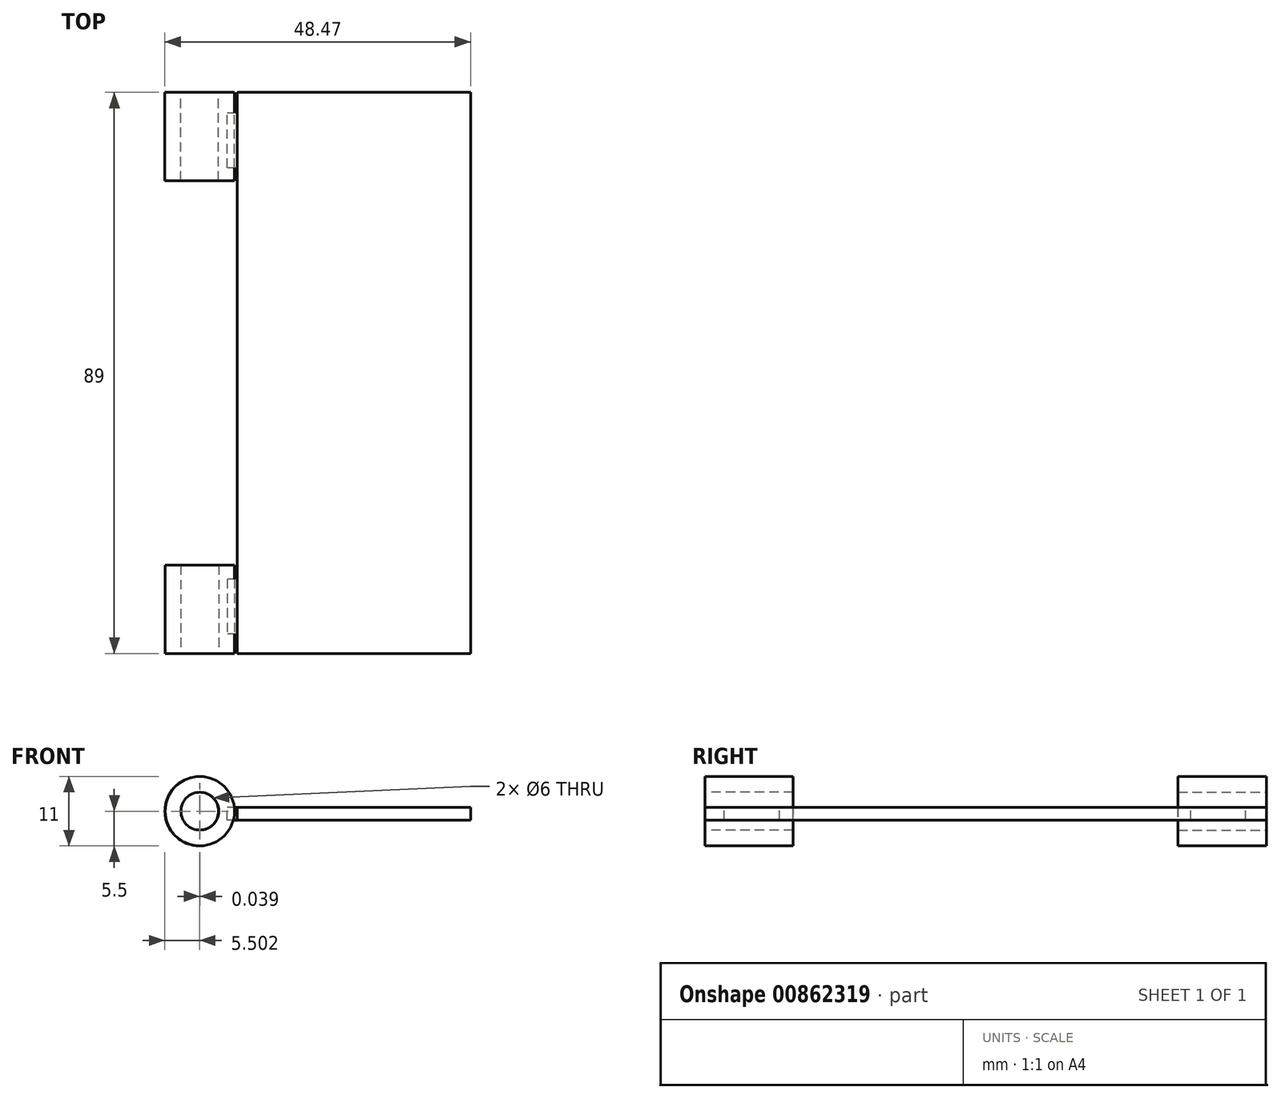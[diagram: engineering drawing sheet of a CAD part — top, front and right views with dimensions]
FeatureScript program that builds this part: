
annotation { "Feature Type Name" : "Feature", "Feature Type Description" : "" }
export const myFeature = defineFeature(function(context is Context, id is Id, definition is map)
    precondition{}
    {
        {
            var Q0;
            Q0=qCreatedBy(makeId("Top.planeOp"),FACE);
            var sketch = newSketch(context, id + "F0", { "sketchPlane" : qUnion([Q0])});
            skLineSegment(sketch, "E0.bottom", {"start": v(0, 0) * mm, "end": v(37, 0) * mm});
            skLineSegment(sketch, "E0.top", {"start": v(0, -89) * mm, "end": v(37, -89) * mm});
            skLineSegment(sketch, "E0.left", {"start": v(0, 0) * mm, "end": v(0, -89) * mm});
            skLineSegment(sketch, "E0.right", {"start": v(37, 0) * mm, "end": v(37, -89) * mm});
            skSolve(sketch);
        }
        {
            var Q0;
            Q0 = qSketchRegion(id + "F0", true);
            extrude(context, id + "F1", {"entities" : qUnion([Q0]), "depth" : 2 * mm, "offsetDistance" : 25 * mm});
        }
        {
            var Q0;
            Q0=makeQuery(id+"F1.opExtrude","SWEPT_FACE",FACE,{"disambiguationData":[OSD([sQuery(id+"F0.wireOp",EDGE,"E0.top")])]});
            var sketch = newSketch(context, id + "F2", { "sketchPlane" : qUnion([Q0])});
            skCircle(sketch, "E1", {"center": v(-5.93, 1.42) * mm, "radius": 5.5 * mm});
            skCircle(sketch, "E2", {"center": v(-5.93, 1.42) * mm, "radius": 3 * mm});
            skLineSegment(sketch, "E3", {"start": v(0, 1.42) * mm, "end": v(0, 2) * mm, "construction": true});
            skSolve(sketch);
        }
        {
            var Q0;
            Q0 = qSketchRegion(id + "F2", true);
            extrude(context, id + "F3", {"entities" : qUnion([Q0]), "oppositeDirection" : true, "depth" : 14 * mm, "offsetDistance" : 25 * mm});
        }
        {
            var Q0;
            Q0=makeQuery(id+"F1.opExtrude","CAP_FACE",FACE,{"disambiguationData":[OSD([sQuery(id+"F0.wireOp",EDGE,"E0.bottom"),sQuery(id+"F0.wireOp",EDGE,"E0.top"),sQuery(id+"F0.wireOp",EDGE,"E0.left"),sQuery(id+"F0.wireOp",EDGE,"E0.right")])],"isStart":false});
            var sketch = newSketch(context, id + "F4", { "sketchPlane" : qUnion([Q0])});
            skLineSegment(sketch, "E4", {"start": v(0, -85.93) * mm, "end": v(-1.59, -85.93) * mm});
            skLineSegment(sketch, "E5", {"start": v(0, -77.2) * mm, "end": v(-1.59, -77.2) * mm});
            skLineSegment(sketch, "E6", {"start": v(-1.59, -77.2) * mm, "end": v(-1.59, -85.93) * mm});
            skLineSegment(sketch, "E7", {"start": v(0, -44.5) * mm, "end": v(37, -44.5) * mm, "construction": true});
            skLineSegment(sketch, "E8.MirrorCS", {"start": v(-1.59, -11.8) * mm, "end": v(-1.59, -3.07) * mm});
            skLineSegment(sketch, "E9.MirrorCS", {"start": v(0, -11.8) * mm, "end": v(-1.59, -11.8) * mm});
            skLineSegment(sketch, "E10.MirrorCS", {"start": v(0, -3.07) * mm, "end": v(-1.59, -3.07) * mm});
            skSolve(sketch);
        }
        {
            var Q0;
            Q0 = qSketchRegion(id + "F4", true);
            var Q1;
            {var subQ0=sQuery(id+"F4.wireOp",EDGE,"E4");Q1=makeQuery(id+"F4.imprint","IMPRINT",FACE,{"disambiguationData":[TD([[makeQuery(id+"F4.imprint","IMPRINT",EDGE,{"derivedFrom":subQ0}),-1.0]])]});}
            extrude(context, id + "F5", {"entities" : qUnion([Q0, Q1]), "oppositeDirection" : true, "depth" : 2 * mm, "offsetDistance" : 25 * mm});
        }
        {
            var Q0;
            Q0=makeQuery(id+"F1.opExtrude","SWEPT_FACE",FACE,{"disambiguationData":[OSD([sQuery(id+"F0.wireOp",EDGE,"E0.bottom")])]});
            var sketch = newSketch(context, id + "F6", { "sketchPlane" : qUnion([Q0])});
            skLineSegment(sketch, "E11", {"start": v(0, 2) * mm, "end": v(0, 1.42) * mm, "construction": true});
            skPoint(sketch, "E11.endSnap0", {"position": v(0, 1) * mm});
            skCircle(sketch, "E12", {"center": v(5.97, 1.42) * mm, "radius": 5.5 * mm});
            skCircle(sketch, "E13", {"center": v(5.97, 1.42) * mm, "radius": 3 * mm});
            skSolve(sketch);
        }
        {
            var Q0;
            Q0 = qSketchRegion(id + "F6", true);
            var Q1;
            Q1 = qSketchRegion(id + "F4", true);
            extrude(context, id + "F7", {"entities" : qUnion([Q0, Q1]), "oppositeDirection" : true, "depth" : 14 * mm, "offsetDistance" : 25 * mm});
        }
        {
            var Q0;
            Q0=makeQuery(id+"F1.opExtrude","CAP_FACE",FACE,{"disambiguationData":[OSD([sQuery(id+"F0.wireOp",EDGE,"E0.bottom"),sQuery(id+"F0.wireOp",EDGE,"E0.top"),sQuery(id+"F0.wireOp",EDGE,"E0.left"),sQuery(id+"F0.wireOp",EDGE,"E0.right")])],"isStart":false});
            var sketch = newSketch(context, id + "F8", { "sketchPlane" : qUnion([Q0])});
            skLineSegment(sketch, "E14", {"start": v(0, -11.98) * mm, "end": v(-1.6, -11.98) * mm});
            skLineSegment(sketch, "E15", {"start": v(-1.6, -11.98) * mm, "end": v(-1.6, -3.24) * mm});
            skLineSegment(sketch, "E16", {"start": v(-1.6, -3.24) * mm, "end": v(0, -3.24) * mm});
            skSolve(sketch);
        }
        {
            var Q0;
            Q0 = qSketchRegion(id + "F8", true);
            var Q1;
            {var subQ0=sQuery(id+"F8.wireOp",EDGE,"E14");Q1=makeQuery(id+"F8.imprint","IMPRINT",FACE,{"disambiguationData":[TD([[makeQuery(id+"F8.imprint","IMPRINT",EDGE,{"derivedFrom":subQ0}),-1.0]])]});}
            extrude(context, id + "F9", {"entities" : qUnion([Q0, Q1]), "oppositeDirection" : true, "depth" : 2 * mm, "offsetDistance" : 25 * mm});
        }
    });
